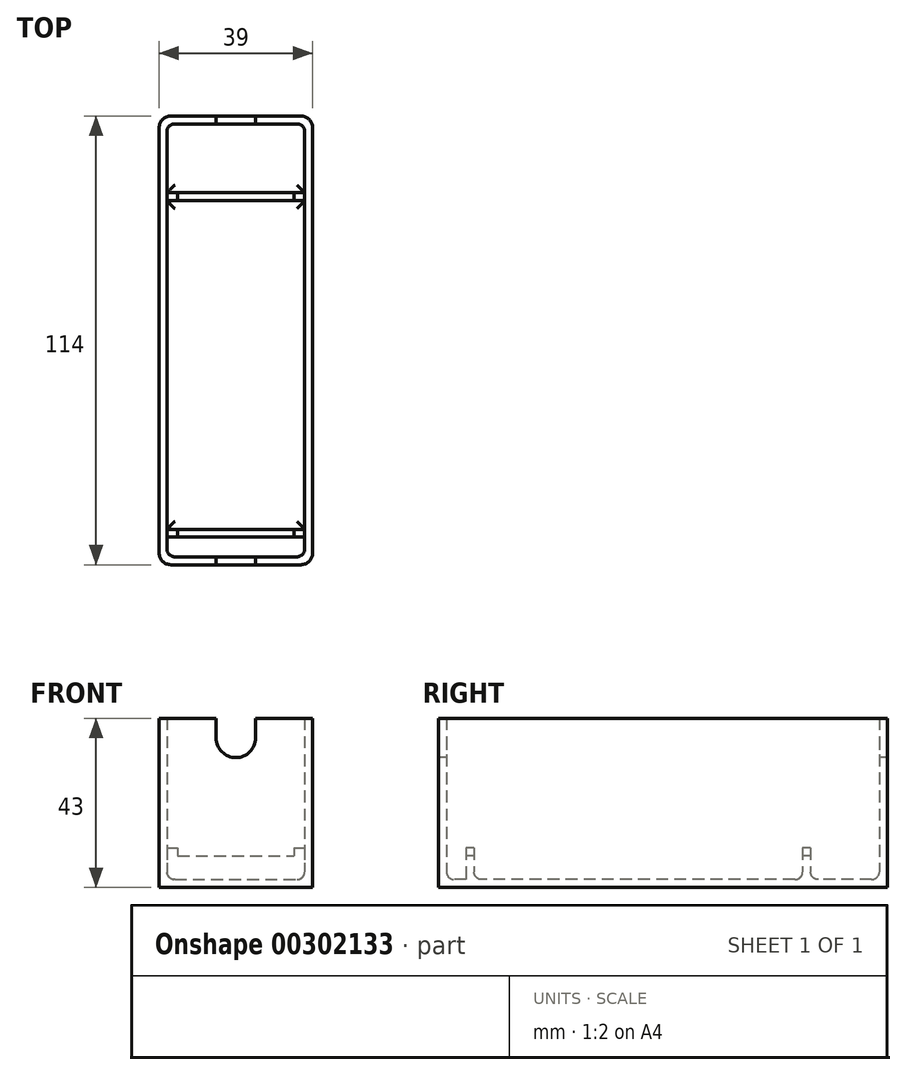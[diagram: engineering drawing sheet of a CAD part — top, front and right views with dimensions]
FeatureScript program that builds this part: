
annotation { "Feature Type Name" : "Feature", "Feature Type Description" : "" }
export const myFeature = defineFeature(function(context is Context, id is Id, definition is map)
    precondition{}
    {
        {
            assignVariable(context, id + "F0", {"name" : "thickness", "anyValue" : 2});
        }
        {
            assignVariable(context, id + "F1", {"name" : "height", "anyValue" : 35});
        }
        {
            assignVariable(context, id + "F2", {"name" : "standOffHeight", "anyValue" : 6});
        }
        {
            assignVariable(context, id + "F3", {"name" : "exteriorHeight", "anyValue" : getVariable(context, 'height') + getVariable(context, 'thickness') + getVariable(context, 'standOffHeight')});
        }
        {
            var Q0;
            Q0=qCreatedBy(makeId("Top.planeOp"),FACE);
            var sketch = newSketch(context, id + "F4", { "sketchPlane" : qUnion([Q0])});
            skLineSegment(sketch, "E0.bottom", {"start": v(19.5, 57) * mm, "end": v(-19.5, 57) * mm});
            skLineSegment(sketch, "E0.top", {"start": v(19.5, -57) * mm, "end": v(-19.5, -57) * mm});
            skLineSegment(sketch, "E0.left", {"start": v(19.5, 57) * mm, "end": v(19.5, -57) * mm});
            skLineSegment(sketch, "E0.right", {"start": v(-19.5, 57) * mm, "end": v(-19.5, -57) * mm});
            skPoint(sketch, "E0.middle", {"position": v(0, 0) * mm});
            skSolve(sketch);
        }
        {
            var Q0;
            Q0 = qSketchRegion(id + "F4", true);
            extrude(context, id + "F5", {"entities" : qUnion([Q0]), "depth" : (getVariable(context, 'exteriorHeight')) * mm});
        }
        {
            var Q0;
            Q0=makeQuery(id+"F5.opExtrude","CAP_FACE",FACE,{"disambiguationData":[OSD([sQuery(id+"F4.wireOp",EDGE,"E0.bottom"),sQuery(id+"F4.wireOp",EDGE,"E0.top"),sQuery(id+"F4.wireOp",EDGE,"E0.left"),sQuery(id+"F4.wireOp",EDGE,"E0.right")])],"isStart":false});
            shell(context, id + "F6", {"entities" : qUnion([Q0]), "thickness" : (getVariable(context, 'thickness')) * mm});
        }
        {
            var Q0;
            Q0=makeQuery(id+"F6.opShell","OFFSET_FACE",FACE,{"disambiguationData":[OSD([sQuery(id+"F4.wireOp",EDGE,"E0.bottom"),sQuery(id+"F4.wireOp",EDGE,"E0.top"),sQuery(id+"F4.wireOp",EDGE,"E0.left"),sQuery(id+"F4.wireOp",EDGE,"E0.right")])]});
            var sketch = newSketch(context, id + "F7", { "sketchPlane" : qUnion([Q0])});
            skLineSegment(sketch, "E1.bottom", {"start": v(-17.5, 55) * mm, "end": v(17.5, 55) * mm});
            skLineSegment(sketch, "E1.top", {"start": v(-17.5, 20) * mm, "end": v(17.5, 20) * mm});
            skLineSegment(sketch, "E1.left", {"start": v(-17.5, 55) * mm, "end": v(-17.5, 20) * mm});
            skLineSegment(sketch, "E1.right", {"start": v(17.5, 55) * mm, "end": v(17.5, 20) * mm});
            skLineSegment(sketch, "E2.top", {"start": v(-17.5, 37.5) * mm, "end": v(17.5, 37.5) * mm});
            skLineSegment(sketch, "E2.left", {"start": v(-17.5, 55) * mm, "end": v(-17.5, 37.5) * mm});
            skLineSegment(sketch, "E2.right", {"start": v(17.5, 55) * mm, "end": v(17.5, 37.5) * mm});
            skLineSegment(sketch, "E3.top", {"start": v(-17.5, 35.5) * mm, "end": v(17.5, 35.5) * mm});
            skLineSegment(sketch, "E3.left", {"start": v(-17.5, 37.5) * mm, "end": v(-17.5, 35.5) * mm});
            skLineSegment(sketch, "E3.right", {"start": v(17.5, 37.5) * mm, "end": v(17.5, 35.5) * mm});
            skLineSegment(sketch, "E4.bottom", {"start": v(-17.5, -55) * mm, "end": v(17.5, -55) * mm});
            skLineSegment(sketch, "E4.top", {"start": v(-17.5, -50) * mm, "end": v(17.5, -50) * mm});
            skLineSegment(sketch, "E4.left", {"start": v(-17.5, -55) * mm, "end": v(-17.5, -50) * mm});
            skLineSegment(sketch, "E4.right", {"start": v(17.5, -55) * mm, "end": v(17.5, -50) * mm});
            skLineSegment(sketch, "E5.top", {"start": v(-17.5, -48) * mm, "end": v(17.5, -48) * mm});
            skLineSegment(sketch, "E5.left", {"start": v(-17.5, -50) * mm, "end": v(-17.5, -48) * mm});
            skLineSegment(sketch, "E5.right", {"start": v(17.5, -50) * mm, "end": v(17.5, -48) * mm});
            skSolve(sketch);
        }
        {
            var Q0;
            Q0=makeQuery(id+"F7.imprint","IMPRINT",FACE,{"disambiguationData":[TD([[makeQuery(id+"F7.imprint","IMPRINT",EDGE,{"derivedFrom":sQuery(id+"F7.wireOp",EDGE,"E2.top")}),-1.0]])]});
            var Q1;
            Q1=makeQuery(id+"F7.imprint","IMPRINT",FACE,{"disambiguationData":[TD([[makeQuery(id+"F7.imprint","IMPRINT",EDGE,{"derivedFrom":sQuery(id+"F7.wireOp",EDGE,"E4.top")}),1.0]])]});
            extrude(context, id + "F8", {"entities" : qUnion([Q0, Q1]), "operationType" : NewBodyOperationType.ADD, "depth" : (getVariable(context, 'standOffHeight')) * mm});
        }
        {
            var Q0;
            Q0=makeQuery(id+"F8.opExtrude","CAP_FACE",FACE,{"disambiguationData":[OSD([sQuery(id+"F7.wireOp",EDGE,"E2.top"),sQuery(id+"F7.wireOp",EDGE,"E3.top"),sQuery(id+"F7.wireOp",EDGE,"E3.left"),sQuery(id+"F7.wireOp",EDGE,"E3.right")])],"isStart":false});
            var sketch = newSketch(context, id + "F9", { "sketchPlane" : qUnion([Q0])});
            skLineSegment(sketch, "E6.bottom", {"start": v(14.75, 37.5) * mm, "end": v(-14.75, 37.5) * mm});
            skLineSegment(sketch, "E6.top", {"start": v(14.75, 35.5) * mm, "end": v(-14.75, 35.5) * mm});
            skLineSegment(sketch, "E6.left", {"start": v(14.75, 37.5) * mm, "end": v(14.75, 35.5) * mm});
            skLineSegment(sketch, "E6.right", {"start": v(-14.75, 37.5) * mm, "end": v(-14.75, 35.5) * mm});
            skPoint(sketch, "E6.middle", {"position": v(0, 36.5) * mm});
            skPoint(sketch, "E6.middle.positionSnap0", {"position": v(0, 35.5) * mm});
            skPoint(sketch, "E6.middle.positionSnap1", {"position": v(-17.5, 36.5) * mm});
            skPoint(sketch, "E6.centerSnap0", {"position": v(0, 35.5) * mm});
            skPoint(sketch, "E6.centerSnap1", {"position": v(-17.5, 36.5) * mm});
            skPoint(sketch, "E7", {"position": v(-17.5, -48) * mm});
            skPoint(sketch, "E8", {"position": v(-17.5, -50) * mm});
            skLineSegment(sketch, "E9", {"start": v(-17.5, -48) * mm, "end": v(-17.5, -50) * mm, "construction": true});
            skLineSegment(sketch, "E10.bottom", {"start": v(14.75, -48) * mm, "end": v(-14.75, -48) * mm});
            skLineSegment(sketch, "E10.top", {"start": v(14.75, -50) * mm, "end": v(-14.75, -50) * mm});
            skLineSegment(sketch, "E10.left", {"start": v(14.75, -48) * mm, "end": v(14.75, -50) * mm});
            skLineSegment(sketch, "E10.right", {"start": v(-14.75, -48) * mm, "end": v(-14.75, -50) * mm});
            skPoint(sketch, "E10.middle", {"position": v(0, -49) * mm});
            skPoint(sketch, "E10.middle.positionSnap0", {"position": v(-17.5, -49) * mm});
            skPoint(sketch, "E10.centerSnap0", {"position": v(-17.5, -49) * mm});
            skLineSegment(sketch, "E11.bottom", {"start": v(-14.75, -48) * mm, "end": v(-17.5, -48) * mm});
            skLineSegment(sketch, "E11.top", {"start": v(-14.75, -50) * mm, "end": v(-17.5, -50) * mm});
            skLineSegment(sketch, "E11.right", {"start": v(-17.5, -48) * mm, "end": v(-17.5, -50) * mm});
            skLineSegment(sketch, "E12.bottom", {"start": v(14.75, -48) * mm, "end": v(17.5, -48) * mm});
            skLineSegment(sketch, "E12.top", {"start": v(14.75, -50) * mm, "end": v(17.5, -50) * mm});
            skLineSegment(sketch, "E12.right", {"start": v(17.5, -48) * mm, "end": v(17.5, -50) * mm});
            skSolve(sketch);
        }
        {
            var Q0;
            {var subQ0=sQuery(id+"F9.wireOp",EDGE,"E6.right");Q0=makeQuery(id+"F9.imprint","IMPRINT",FACE,{"disambiguationData":[TD([[makeQuery(id+"F9.imprint","IMPRINT",EDGE,{"derivedFrom":subQ0}),-1.0]])]});}
            var Q1;
            {var subQ0=sQuery(id+"F9.wireOp",EDGE,"E6.left");Q1=makeQuery(id+"F9.imprint","IMPRINT",FACE,{"disambiguationData":[TD([[makeQuery(id+"F9.imprint","IMPRINT",EDGE,{"derivedFrom":subQ0}),1.0]])]});}
            var Q2;
            Q2=makeQuery(id+"F9.imprint","IMPRINT",FACE,{"disambiguationData":[TD([[makeQuery(id+"F9.imprint","IMPRINT",EDGE,{"derivedFrom":sQuery(id+"F9.wireOp",EDGE,"E11.bottom")}),1.0]])]});
            var Q3;
            Q3=makeQuery(id+"F9.imprint","IMPRINT",FACE,{"disambiguationData":[TD([[makeQuery(id+"F9.imprint","IMPRINT",EDGE,{"derivedFrom":sQuery(id+"F9.wireOp",EDGE,"E12.bottom")}),-1.0]])]});
            extrude(context, id + "F10", {"entities" : qUnion([Q0, Q1, Q2, Q3]), "operationType" : NewBodyOperationType.ADD, "depth" : 2 * mm});
        }
        {
            var Q0;
            Q0=makeQuery(id+"F6.opShell","OFFSET_EDGE",EDGE,{"disambiguationData":[OSD([sQuery(id+"F4.wireOp",EDGE,"E0.bottom"),sQuery(id+"F4.wireOp",EDGE,"E0.right")])]});
            var Q1;
            {var subQ0=sQuery(id+"F4.wireOp",EDGE,"E0.bottom");var subQ1=sQuery(id+"F4.wireOp",EDGE,"E0.right");Q1=makeQuery(id+"F8.boolean.opBoolean","SPLIT",EDGE,{"disambiguationData":[TD([makeQuery(id+"F6.opShell","OFFSET_FACE",FACE,{"disambiguationData":[OSD([subQ0])]})])],"derivedFrom":makeQuery(id+"F6.opShell","OFFSET_EDGE",EDGE,{"disambiguationData":[OSD([subQ1]),TDD([makeQuery(id+"F5.opExtrude","CAP_EDGE",EDGE,{"disambiguationData":[OSD([subQ1])],"isStart":true})])]})});}
            var Q2;
            {var subQ0=sQuery(id+"F4.wireOp",EDGE,"E0.bottom");Q2=makeQuery(id+"F6.opShell","OFFSET_EDGE",EDGE,{"disambiguationData":[OSD([subQ0]),TDD([makeQuery(id+"F5.opExtrude","CAP_EDGE",EDGE,{"disambiguationData":[OSD([subQ0])],"isStart":true})])]});}
            var Q3;
            {var subQ0=sQuery(id+"F4.wireOp",EDGE,"E0.right");Q3=makeQuery(id+"F8.boolean.opBoolean","SPLIT",EDGE,{"disambiguationData":[TD([makeQuery(id+"F8.opExtrude","SWEPT_FACE",FACE,{"disambiguationData":[OSD([sQuery(id+"F7.wireOp",EDGE,"E3.top")])]})])],"derivedFrom":makeQuery(id+"F6.opShell","OFFSET_EDGE",EDGE,{"disambiguationData":[OSD([subQ0]),TDD([makeQuery(id+"F5.opExtrude","CAP_EDGE",EDGE,{"disambiguationData":[OSD([subQ0])],"isStart":true})])]})});}
            var Q4;
            Q4=makeQuery(id+"F8.opExtrude","CAP_EDGE",EDGE,{"disambiguationData":[OSD([sQuery(id+"F7.wireOp",EDGE,"E5.top")])],"isStart":true});
            var Q5;
            {var subQ0=sQuery(id+"F4.wireOp",EDGE,"E0.right");var subQ1=sQuery(id+"F4.wireOp",EDGE,"E0.top");Q5=makeQuery(id+"F8.boolean.opBoolean","SPLIT",EDGE,{"disambiguationData":[TD([makeQuery(id+"F6.opShell","OFFSET_FACE",FACE,{"disambiguationData":[OSD([subQ1])]})])],"derivedFrom":makeQuery(id+"F6.opShell","OFFSET_EDGE",EDGE,{"disambiguationData":[OSD([subQ0]),TDD([makeQuery(id+"F5.opExtrude","CAP_EDGE",EDGE,{"disambiguationData":[OSD([subQ0])],"isStart":true})])]})});}
            var Q6;
            Q6=makeQuery(id+"F8.opExtrude","CAP_EDGE",EDGE,{"disambiguationData":[OSD([sQuery(id+"F7.wireOp",EDGE,"E4.top")])],"isStart":true});
            var Q7;
            {var subQ0=sQuery(id+"F4.wireOp",EDGE,"E0.top");Q7=makeQuery(id+"F6.opShell","OFFSET_EDGE",EDGE,{"disambiguationData":[OSD([subQ0]),TDD([makeQuery(id+"F5.opExtrude","CAP_EDGE",EDGE,{"disambiguationData":[OSD([subQ0])],"isStart":true})])]});}
            var Q8;
            Q8=makeQuery(id+"F6.opShell","OFFSET_EDGE",EDGE,{"disambiguationData":[OSD([sQuery(id+"F4.wireOp",EDGE,"E0.top"),sQuery(id+"F4.wireOp",EDGE,"E0.right")])]});
            var Q9;
            Q9=makeQuery(id+"F6.opShell","OFFSET_EDGE",EDGE,{"disambiguationData":[OSD([sQuery(id+"F4.wireOp",EDGE,"E0.top"),sQuery(id+"F4.wireOp",EDGE,"E0.left")])]});
            var Q10;
            {var subQ0=sQuery(id+"F4.wireOp",EDGE,"E0.left");var subQ1=sQuery(id+"F4.wireOp",EDGE,"E0.top");Q10=makeQuery(id+"F8.boolean.opBoolean","SPLIT",EDGE,{"disambiguationData":[TD([makeQuery(id+"F6.opShell","OFFSET_FACE",FACE,{"disambiguationData":[OSD([subQ1])]})])],"derivedFrom":makeQuery(id+"F6.opShell","OFFSET_EDGE",EDGE,{"disambiguationData":[OSD([subQ0]),TDD([makeQuery(id+"F5.opExtrude","CAP_EDGE",EDGE,{"disambiguationData":[OSD([subQ0])],"isStart":true})])]})});}
            var Q11;
            {var subQ0=sQuery(id+"F4.wireOp",EDGE,"E0.left");Q11=makeQuery(id+"F8.boolean.opBoolean","SPLIT",EDGE,{"disambiguationData":[TD([makeQuery(id+"F8.opExtrude","SWEPT_FACE",FACE,{"disambiguationData":[OSD([sQuery(id+"F7.wireOp",EDGE,"E3.top")])]})])],"derivedFrom":makeQuery(id+"F6.opShell","OFFSET_EDGE",EDGE,{"disambiguationData":[OSD([subQ0]),TDD([makeQuery(id+"F5.opExtrude","CAP_EDGE",EDGE,{"disambiguationData":[OSD([subQ0])],"isStart":true})])]})});}
            var Q12;
            Q12=makeQuery(id+"F8.opExtrude","CAP_EDGE",EDGE,{"disambiguationData":[OSD([sQuery(id+"F7.wireOp",EDGE,"E2.top")])],"isStart":true});
            var Q13;
            Q13=makeQuery(id+"F8.opExtrude","CAP_EDGE",EDGE,{"disambiguationData":[OSD([sQuery(id+"F7.wireOp",EDGE,"E3.top")])],"isStart":true});
            var Q14;
            {var subQ0=sQuery(id+"F4.wireOp",EDGE,"E0.bottom");var subQ1=sQuery(id+"F4.wireOp",EDGE,"E0.left");Q14=makeQuery(id+"F8.boolean.opBoolean","SPLIT",EDGE,{"disambiguationData":[TD([makeQuery(id+"F6.opShell","OFFSET_FACE",FACE,{"disambiguationData":[OSD([subQ0])]})])],"derivedFrom":makeQuery(id+"F6.opShell","OFFSET_EDGE",EDGE,{"disambiguationData":[OSD([subQ1]),TDD([makeQuery(id+"F5.opExtrude","CAP_EDGE",EDGE,{"disambiguationData":[OSD([subQ1])],"isStart":true})])]})});}
            var Q15;
            Q15=makeQuery(id+"F6.opShell","OFFSET_EDGE",EDGE,{"disambiguationData":[OSD([sQuery(id+"F4.wireOp",EDGE,"E0.bottom"),sQuery(id+"F4.wireOp",EDGE,"E0.left")])]});
            fillet(context, id + "F11", {"entities" : qUnion([Q0, Q1, Q2, Q3, Q4, Q5, Q6, Q7, Q8, Q9, Q10, Q11, Q12, Q13, Q14, Q15]), "radius" : 2 * mm, "tangentPropagation" : true, "allowEdgeOverflow" : false});
        }
        {
            var Q0;
            Q0=makeQuery(id+"F5.opExtrude","SWEPT_FACE",FACE,{"disambiguationData":[OSD([sQuery(id+"F4.wireOp",EDGE,"E0.top")])]});
            var sketch = newSketch(context, id + "F12", { "sketchPlane" : qUnion([Q0])});
            skLineSegment(sketch, "E13.top", {"start": v(5, 33) * mm, "end": v(-5, 33) * mm});
            skPoint(sketch, "E13.middle", {"position": v(0, 43) * mm});
            skLineSegment(sketch, "E14.bottom", {"start": v(-5, 43) * mm, "end": v(5, 43) * mm});
            skLineSegment(sketch, "E14.left", {"start": v(-5, 43) * mm, "end": v(-5, 33) * mm});
            skLineSegment(sketch, "E14.right", {"start": v(5, 43) * mm, "end": v(5, 33) * mm});
            skCircle(sketch, "E15", {"center": v(0, 38) * mm, "radius": 5 * mm});
            skPoint(sketch, "E15.centerSnap0", {"position": v(-5, 38) * mm});
            skSolve(sketch);
        }
        {
            var Q0;
            {var subQ1=sQuery(id+"F12.wireOp",EDGE,"E14.bottom");var subQ3=sQuery(id+"F12.wireOp",EDGE,"E15");var subQ4=makeQuery(id+"F12.imprint","INTERSECT",VERTEX,{"derivedFrom":[subQ1,subQ3]});Q0=makeQuery(id+"F12.imprint","IMPRINT",FACE,{"disambiguationData":[TD([[makeQuery(id+"F12.imprint","IMPRINT",EDGE,{"disambiguationData":[TD([[subQ4,-1.0]])],"derivedFrom":subQ3}),-1.0]])]});}
            var Q1;
            {var subQ0=sQuery(id+"F12.wireOp",EDGE,"E15");var subQ1=makeQuery(id+"F12.imprint","INTERSECT",VERTEX,{"derivedFrom":[sQuery(id+"F12.wireOp",EDGE,"E14.bottom"),subQ0]});Q1=makeQuery(id+"F12.imprint","IMPRINT",FACE,{"disambiguationData":[TD([[makeQuery(id+"F12.imprint","IMPRINT",EDGE,{"disambiguationData":[TD([[subQ1,1.0]])],"derivedFrom":subQ0}),1.0]])]});}
            var Q2;
            {var subQ1=sQuery(id+"F12.wireOp",EDGE,"E14.bottom");var subQ3=sQuery(id+"F12.wireOp",EDGE,"E15");var subQ4=makeQuery(id+"F12.imprint","INTERSECT",VERTEX,{"derivedFrom":[subQ1,subQ3]});Q2=makeQuery(id+"F12.imprint","IMPRINT",FACE,{"disambiguationData":[TD([[makeQuery(id+"F12.imprint","IMPRINT",EDGE,{"disambiguationData":[TD([[subQ4,1.0]])],"derivedFrom":subQ3}),-1.0]])]});}
            extrude(context, id + "F13", {"entities" : qUnion([Q0, Q1, Q2]), "operationType" : NewBodyOperationType.REMOVE, "endBound" : BoundingType.THROUGH_ALL, "oppositeDirection" : true, "depth" : 25 * mm});
        }
        {
            var Q0;
            Q0=makeQuery(id+"F5.opExtrude","SWEPT_EDGE",EDGE,{"disambiguationData":[OSD([sQuery(id+"F4.wireOp",EDGE,"E0.top"),sQuery(id+"F4.wireOp",EDGE,"E0.left")])]});
            var Q1;
            Q1=makeQuery(id+"F5.opExtrude","SWEPT_EDGE",EDGE,{"disambiguationData":[OSD([sQuery(id+"F4.wireOp",EDGE,"E0.bottom"),sQuery(id+"F4.wireOp",EDGE,"E0.left")])]});
            var Q2;
            Q2=makeQuery(id+"F5.opExtrude","SWEPT_EDGE",EDGE,{"disambiguationData":[OSD([sQuery(id+"F4.wireOp",EDGE,"E0.bottom"),sQuery(id+"F4.wireOp",EDGE,"E0.right")])]});
            var Q3;
            Q3=makeQuery(id+"F5.opExtrude","SWEPT_EDGE",EDGE,{"disambiguationData":[OSD([sQuery(id+"F4.wireOp",EDGE,"E0.top"),sQuery(id+"F4.wireOp",EDGE,"E0.right")])]});
            fillet(context, id + "F14", {"entities" : qUnion([Q0, Q1, Q2, Q3]), "radius" : 3 * mm, "tangentPropagation" : true, "allowEdgeOverflow" : false});
        }
    });
